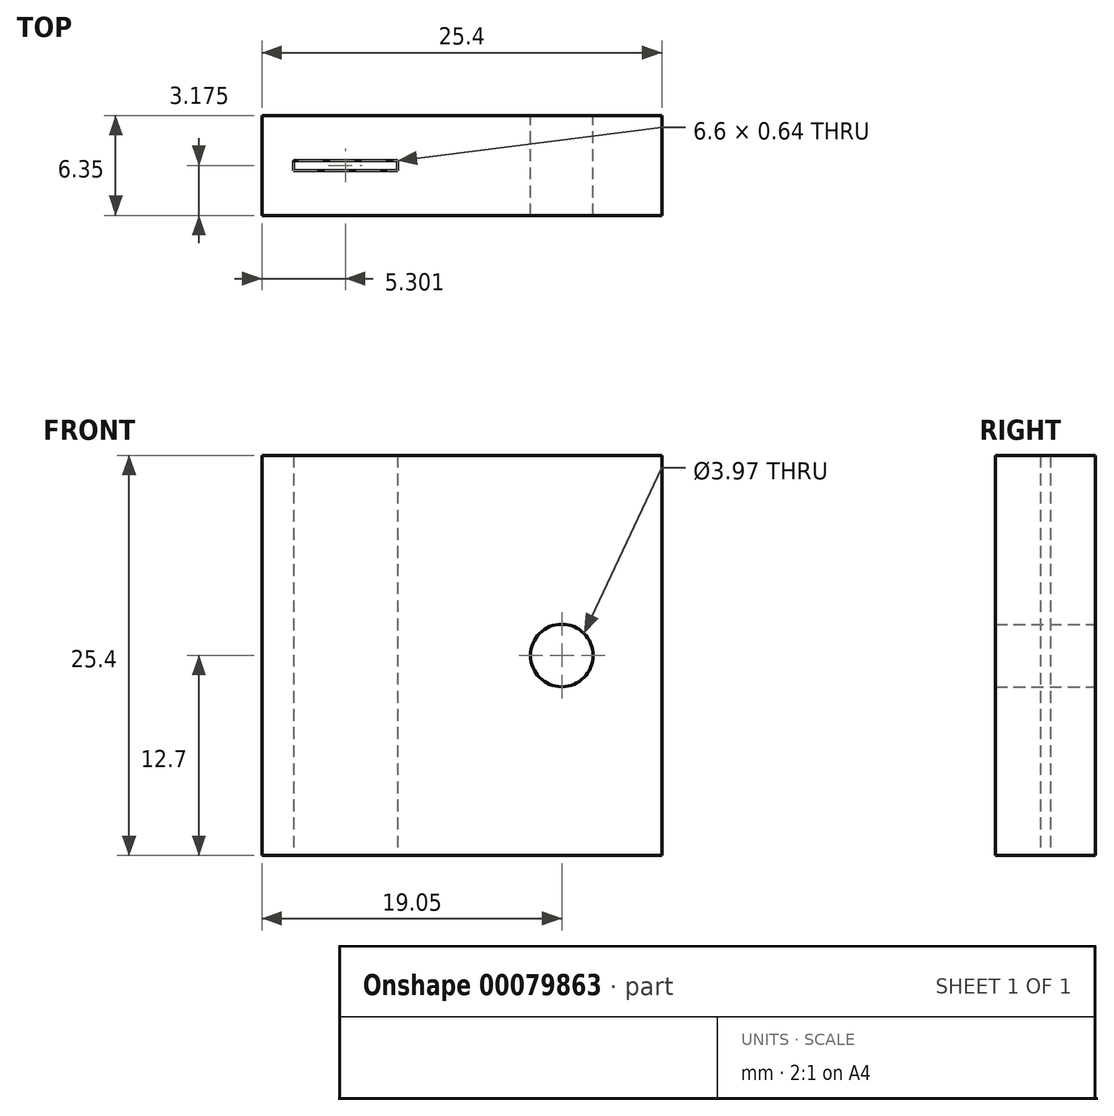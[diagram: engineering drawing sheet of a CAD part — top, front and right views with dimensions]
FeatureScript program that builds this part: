
annotation { "Feature Type Name" : "Feature", "Feature Type Description" : "" }
export const myFeature = defineFeature(function(context is Context, id is Id, definition is map)
    precondition{}
    {
        {
            var Q0;
            Q0=qCreatedBy(makeId("Front.planeOp"),FACE);
            var sketch = newSketch(context, id + "F0", { "sketchPlane" : qUnion([Q0])});
            skLineSegment(sketch, "E0.bottom", {"start": v(0, 0) * mm, "end": v(25.4, 0) * mm});
            skLineSegment(sketch, "E0.top", {"start": v(0, 25.4) * mm, "end": v(25.4, 25.4) * mm});
            skLineSegment(sketch, "E0.left", {"start": v(0, 0) * mm, "end": v(0, 25.4) * mm});
            skLineSegment(sketch, "E0.right", {"start": v(25.4, 0) * mm, "end": v(25.4, 25.4) * mm});
            skCircle(sketch, "E1", {"center": v(19.05, 12.7) * mm, "radius": 1.98 * mm});
            skPoint(sketch, "E1.centerSnap0", {"position": v(0, 12.7) * mm});
            skLineSegment(sketch, "E2", {"start": v(0, 12.7) * mm, "end": v(12.7, 12.7) * mm});
            skSolve(sketch);
        }
        {
            var Q0;
            {var subQ3=sQuery(id+"F0.wireOp",EDGE,"E0.bottom");Q0=makeQuery(id+"F0.imprint","IMPRINT",FACE,{"disambiguationData":[TD([[makeQuery(id+"F0.imprint","IMPRINT",EDGE,{"derivedFrom":subQ3}),1.0]])]});}
            extrude(context, id + "F1", {"entities" : qUnion([Q0]), "depth" : 6.35 * mm});
        }
        {
            var Q0;
            Q0=makeQuery(id+"F1.opExtrude","SWEPT_FACE",FACE,{"disambiguationData":[OSD([sQuery(id+"F0.wireOp",EDGE,"E0.bottom")])]});
            var sketch = newSketch(context, id + "F2", { "sketchPlane" : qUnion([Q0])});
            skLineSegment(sketch, "E3", {"start": v(2, 3.18) * mm, "end": v(8.6, 3.18) * mm});
            skPoint(sketch, "E3.startSnap0", {"position": v(0, 3.18) * mm});
            skLineSegment(sketch, "E4.bottom", {"start": v(2, 3.5) * mm, "end": v(8.6, 3.5) * mm});
            skLineSegment(sketch, "E4.top", {"start": v(2, 2.86) * mm, "end": v(8.6, 2.86) * mm});
            skLineSegment(sketch, "E4.left", {"start": v(2, 3.5) * mm, "end": v(2, 2.86) * mm});
            skLineSegment(sketch, "E4.right", {"start": v(8.6, 3.5) * mm, "end": v(8.6, 2.86) * mm});
            skSolve(sketch);
        }
        {
            var Q0;
            Q0 = qSketchRegion(id + "F2", true);
            extrude(context, id + "F3", {"entities" : qUnion([Q0]), "operationType" : NewBodyOperationType.REMOVE, "oppositeDirection" : true, "depth" : 76.2 * mm});
        }
    });
